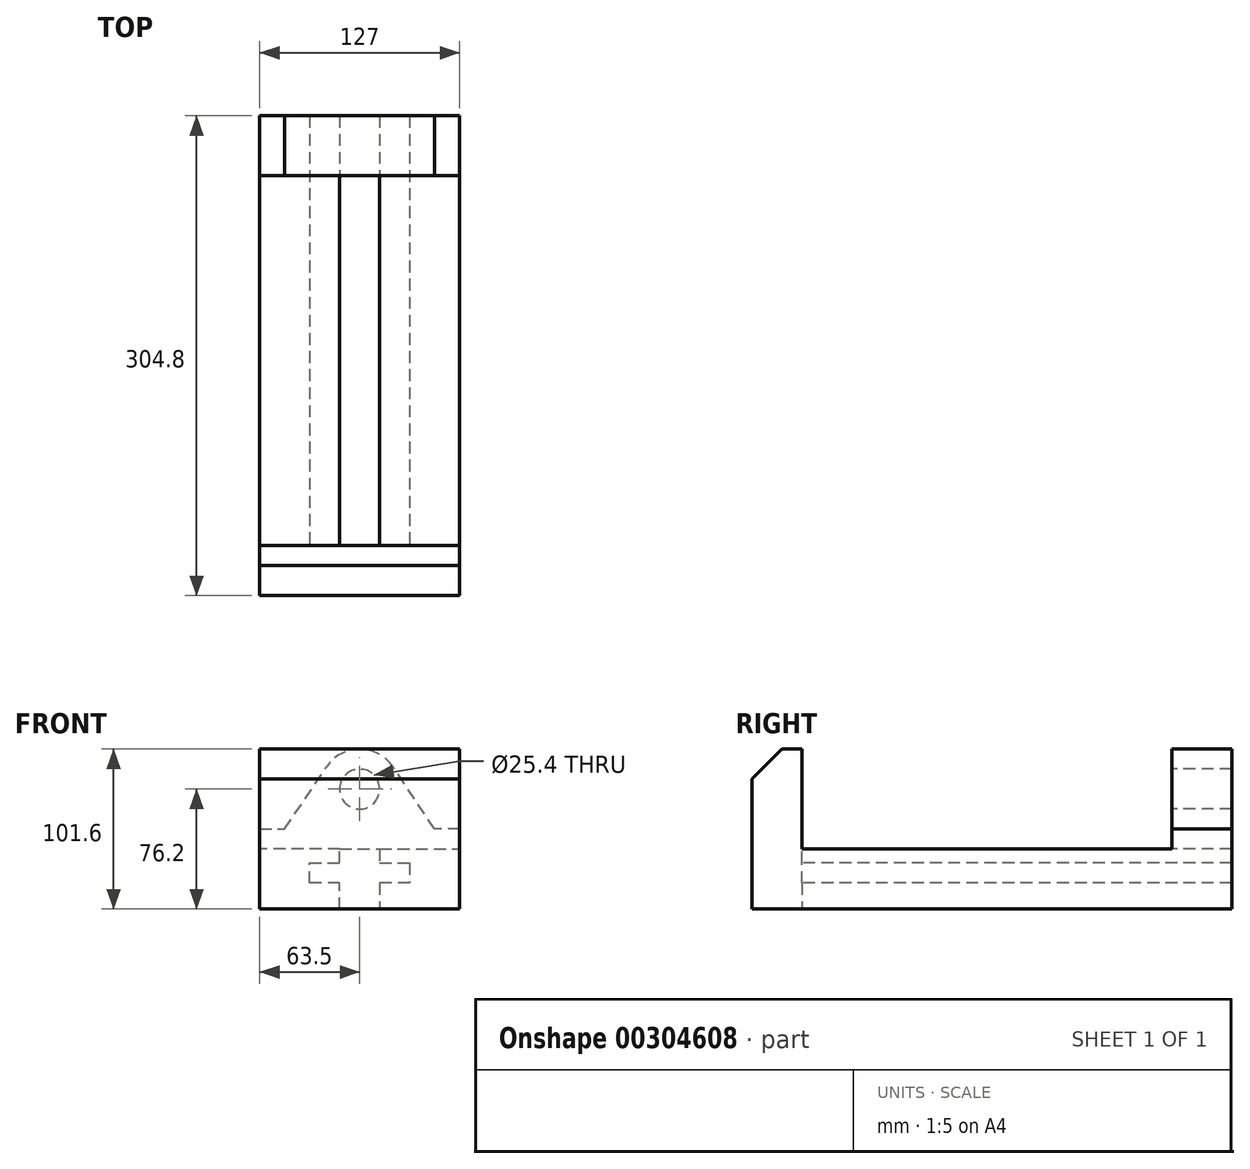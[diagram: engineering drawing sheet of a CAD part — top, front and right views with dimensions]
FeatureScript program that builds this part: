
annotation { "Feature Type Name" : "Feature", "Feature Type Description" : "" }
export const myFeature = defineFeature(function(context is Context, id is Id, definition is map)
    precondition{}
    {
        {
            var Q0;
            Q0=qCreatedBy(makeId("Right.planeOp"),FACE);
            var sketch = newSketch(context, id + "F0", { "sketchPlane" : qUnion([Q0])});
            skLineSegment(sketch, "E0.bottom", {"start": v(0, 0) * mm, "end": v(31.75, 0) * mm});
            skLineSegment(sketch, "E0.top", {"start": v(0, 101.6) * mm, "end": v(31.75, 101.6) * mm});
            skLineSegment(sketch, "E0.left", {"start": v(0, 0) * mm, "end": v(0, 101.6) * mm});
            skLineSegment(sketch, "E0.right", {"start": v(31.75, 0) * mm, "end": v(31.75, 101.6) * mm});
            skSolve(sketch);
        }
        {
            var Q0;
            Q0=makeQuery(id+"F0.imprint","IMPRINT",FACE,{"disambiguationData":[TD([[makeQuery(id+"F0.imprint","IMPRINT",EDGE,{"derivedFrom":sQuery(id+"F0.wireOp",EDGE,"E0.bottom")}),1.0]])]});
            extrude(context, id + "F1", {"entities" : qUnion([Q0]), "depth" : 127 * mm});
        }
        {
            var Q0;
            Q0=makeQuery(id+"F1.opExtrude","SWEPT_EDGE",EDGE,{"disambiguationData":[OSD([sQuery(id+"F0.wireOp",EDGE,"E0.top"),sQuery(id+"F0.wireOp",EDGE,"E0.left")])]});
            chamfer(context, id + "F2", {"entities" : qUnion([Q0]), "width" : 19.05 * mm, "tangentPropagation" : true});
        }
        {
            var Q0;
            Q0=makeQuery(id+"F1.opExtrude","SWEPT_FACE",FACE,{"disambiguationData":[OSD([sQuery(id+"F0.wireOp",EDGE,"E0.right")])]});
            var sketch = newSketch(context, id + "F3", { "sketchPlane" : qUnion([Q0])});
            skPoint(sketch, "E1.centerSnap0", {"position": v(-63.5, 101.6) * mm});
            skLineSegment(sketch, "E2", {"start": v(0, 0) * mm, "end": v(-50.8, 0) * mm});
            skLineSegment(sketch, "E3", {"start": v(-127, 0) * mm, "end": v(-76.2, 0) * mm});
            skLineSegment(sketch, "E4", {"start": v(-50.8, 0) * mm, "end": v(-50.8, 16.5) * mm});
            skLineSegment(sketch, "E5", {"start": v(-50.8, 16.5) * mm, "end": v(-31.75, 16.5) * mm});
            skLineSegment(sketch, "E6", {"start": v(-31.75, 16.5) * mm, "end": v(-31.75, 29.21) * mm});
            skLineSegment(sketch, "E7", {"start": v(-31.75, 29.21) * mm, "end": v(-50.8, 29.21) * mm});
            skLineSegment(sketch, "E8", {"start": v(-50.8, 29.21) * mm, "end": v(-50.8, 38.1) * mm});
            skLineSegment(sketch, "E9", {"start": v(-76.2, 38.1) * mm, "end": v(-76.2, 29.21) * mm});
            skLineSegment(sketch, "E10", {"start": v(-76.2, 29.21) * mm, "end": v(-95.25, 29.21) * mm});
            skLineSegment(sketch, "E11", {"start": v(-95.25, 29.21) * mm, "end": v(-95.25, 16.5) * mm});
            skLineSegment(sketch, "E12", {"start": v(-95.25, 16.5) * mm, "end": v(-76.2, 16.5) * mm});
            skLineSegment(sketch, "E13", {"start": v(-76.2, 16.5) * mm, "end": v(-76.2, 0) * mm});
            skLineSegment(sketch, "E14", {"start": v(-76.2, 38.1) * mm, "end": v(-127, 38.1) * mm});
            skLineSegment(sketch, "E15", {"start": v(-127, 38.1) * mm, "end": v(-127, 0) * mm});
            skLineSegment(sketch, "E16", {"start": v(-50.8, 38.1) * mm, "end": v(0, 38.1) * mm});
            skLineSegment(sketch, "E17", {"start": v(0, 38.1) * mm, "end": v(0, 0) * mm});
            skSolve(sketch);
        }
        {
            var Q0;
            Q0=makeQuery(id+"F3.imprint","IMPRINT",FACE,{"disambiguationData":[TD([[makeQuery(id+"F3.imprint","IMPRINT",EDGE,{"derivedFrom":sQuery(id+"F3.wireOp",EDGE,"E3")}),1.0]])]});
            var Q1;
            Q1=makeQuery(id+"F3.imprint","IMPRINT",FACE,{"disambiguationData":[TD([[makeQuery(id+"F3.imprint","IMPRINT",EDGE,{"derivedFrom":sQuery(id+"F3.wireOp",EDGE,"E2")}),1.0]])]});
            extrude(context, id + "F4", {"entities" : qUnion([Q0, Q1]), "operationType" : NewBodyOperationType.ADD, "depth" : 234.95 * mm});
        }
        {
            var Q0;
            Q0=makeQuery(id+"F4.opExtrude","CAP_FACE",FACE,{"disambiguationData":[OSD([sQuery(id+"F3.wireOp",EDGE,"E3"),sQuery(id+"F3.wireOp",EDGE,"E9"),sQuery(id+"F3.wireOp",EDGE,"E10"),sQuery(id+"F3.wireOp",EDGE,"E11"),sQuery(id+"F3.wireOp",EDGE,"E12"),sQuery(id+"F3.wireOp",EDGE,"E13"),sQuery(id+"F3.wireOp",EDGE,"E14"),sQuery(id+"F3.wireOp",EDGE,"E15")])],"isStart":false});
            var sketch = newSketch(context, id + "F5", { "sketchPlane" : qUnion([Q0])});
            skLineSegment(sketch, "E18", {"start": v(0, 0) * mm, "end": v(-50.8, 0) * mm});
            skLineSegment(sketch, "E19", {"start": v(-50.8, 0) * mm, "end": v(-50.8, 16.5) * mm});
            skLineSegment(sketch, "E20", {"start": v(-50.8, 16.5) * mm, "end": v(-31.75, 16.5) * mm});
            skLineSegment(sketch, "E21", {"start": v(-31.75, 16.5) * mm, "end": v(-31.75, 29.21) * mm});
            skLineSegment(sketch, "E22", {"start": v(-31.75, 29.21) * mm, "end": v(-50.8, 29.21) * mm});
            skLineSegment(sketch, "E23", {"start": v(-50.8, 29.21) * mm, "end": v(-50.8, 38.1) * mm});
            skLineSegment(sketch, "E24", {"start": v(-50.8, 38.1) * mm, "end": v(-76.2, 38.1) * mm});
            skLineSegment(sketch, "E25", {"start": v(-76.2, 38.1) * mm, "end": v(-76.2, 29.21) * mm});
            skLineSegment(sketch, "E26", {"start": v(-76.2, 29.21) * mm, "end": v(-95.25, 29.21) * mm});
            skLineSegment(sketch, "E27", {"start": v(-95.25, 29.21) * mm, "end": v(-95.25, 16.5) * mm});
            skLineSegment(sketch, "E28", {"start": v(-95.25, 16.5) * mm, "end": v(-76.2, 16.5) * mm});
            skLineSegment(sketch, "E29", {"start": v(-76.2, 16.5) * mm, "end": v(-76.2, 0) * mm});
            skLineSegment(sketch, "E30", {"start": v(-76.2, 0) * mm, "end": v(-127, 0) * mm});
            skLineSegment(sketch, "E31", {"start": v(0, 0) * mm, "end": v(0, 50.8) * mm});
            skLineSegment(sketch, "E32", {"start": v(-127, 0) * mm, "end": v(-127, 50.8) * mm});
            skLineSegment(sketch, "E33", {"start": v(-127, 50.8) * mm, "end": v(-111.12, 50.8) * mm});
            skLineSegment(sketch, "E34", {"start": v(-111.12, 50.8) * mm, "end": v(-84.6, 90.35) * mm});
            skLineSegment(sketch, "E35", {"start": v(0, 50.8) * mm, "end": v(-15.88, 50.8) * mm});
            skLineSegment(sketch, "E36", {"start": v(-15.87, 50.8) * mm, "end": v(-42.4, 90.35) * mm});
            skArc(sketch, "E37", {"start": v(-42.4, 90.35) * mm, "mid": v(-63.5, 101.6) * mm, "end": v(-84.6, 90.35) * mm});
            skCircle(sketch, "E38", {"center": v(-63.5, 76.2) * mm, "radius": 12.7 * mm});
            skSolve(sketch);
        }
        {
            var Q0;
            Q0 = qSketchRegion(id + "F5", true);
            extrude(context, id + "F6", {"entities" : qUnion([Q0]), "operationType" : NewBodyOperationType.ADD, "depth" : 38.1 * mm});
        }
    });
